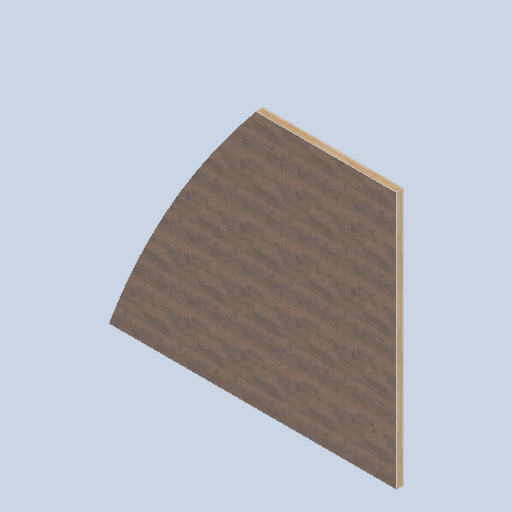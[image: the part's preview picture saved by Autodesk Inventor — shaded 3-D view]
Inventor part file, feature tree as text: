
AUTODESK INVENTOR PART (.ipt)
format: ipt  version: 2024.2 (Build 282272000, 272)  size: 189,952 bytes
history: native  units: in
note: dims shown in document units (in); Inventor stores cm internally (conversion verified against a paired STEP export)
features: other x3, sketch x1
ambient origin geometry x8: Origin, YZ Plane, XZ Plane, XY Plane, X Axis, Y Axis, Z Axis, Center Point
bodies: Solid1 (feature_tree)
feature tree (4):
  other  "front_wall_block02.ipt"
  other  "Solid1::front_wall_block02.ipt"
  other  "TaggingFeature1"
  sketch  "Sketch1"  dims[d0=0.3937in]
